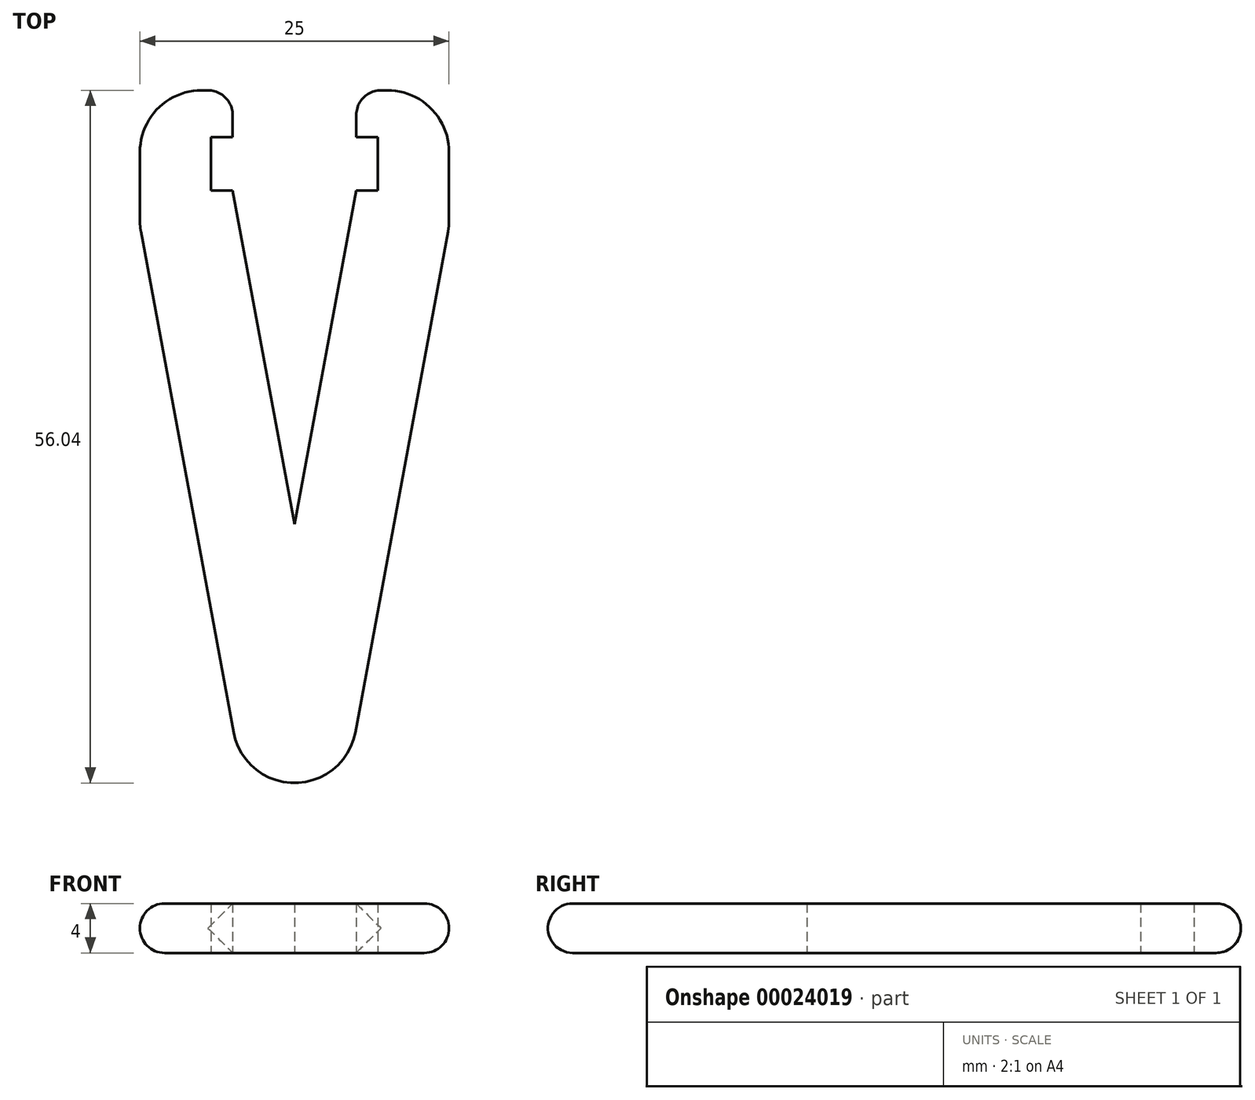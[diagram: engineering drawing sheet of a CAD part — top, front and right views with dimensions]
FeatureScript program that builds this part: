
annotation { "Feature Type Name" : "Feature", "Feature Type Description" : "" }
export const myFeature = defineFeature(function(context is Context, id is Id, definition is map)
    precondition{}
    {
        {
            var Q0;
            Q0=qCreatedBy(makeId("Top.planeOp"),FACE);
            var sketch = newSketch(context, id + "F0", { "sketchPlane" : qUnion([Q0])});
            skLineSegment(sketch, "E0.rect.bottom", {"start": v(6.75, -2.15) * mm, "end": v(-6.75, -2.15) * mm});
            skLineSegment(sketch, "E0.rect.top", {"start": v(6.75, 2.15) * mm, "end": v(-6.75, 2.15) * mm});
            skLineSegment(sketch, "E0.rect.left", {"start": v(6.75, -2.15) * mm, "end": v(6.75, 2.15) * mm});
            skLineSegment(sketch, "E0.rect.right", {"start": v(-6.75, -2.15) * mm, "end": v(-6.75, 2.15) * mm});
            skPoint(sketch, "E0.rect.middle", {"position": v(0, 0) * mm});
            skLineSegment(sketch, "E1", {"start": v(0, -2.15) * mm, "end": v(0, -29.15) * mm, "construction": true});
            skLineSegment(sketch, "E2", {"start": v(0, -2.15) * mm, "end": v(-5, -2.15) * mm});
            skLineSegment(sketch, "E3", {"start": v(0, 0) * mm, "end": v(0, 8.22) * mm, "construction": true});
            skLineSegment(sketch, "E4", {"start": v(0, 0) * mm, "end": v(-18.96, 0) * mm, "construction": true});
            skLineSegment(sketch, "E5.MirrorCS", {"start": v(0, 2.15) * mm, "end": v(-5, 2.15) * mm});
            skLineSegment(sketch, "E6", {"start": v(-5, 2.15) * mm, "end": v(-5, 5.95) * mm});
            skLineSegment(sketch, "E7", {"start": v(-5, -2.15) * mm, "end": v(0, -29.15) * mm});
            skLineSegment(sketch, "E8", {"start": v(-5, 5.95) * mm, "end": v(-12.5, 5.95) * mm});
            skLineSegment(sketch, "E9", {"start": v(-12.5, 5.95) * mm, "end": v(-12.5, -5.05) * mm});
            skLineSegment(sketch, "E10", {"start": v(-12.5, -5.05) * mm, "end": v(0, -72.55) * mm});
            skLineSegment(sketch, "E11", {"start": v(0, -29.15) * mm, "end": v(0, -98.8) * mm, "construction": true});
            skLineSegment(sketch, "E12.MirrorCS", {"start": v(5, -2.15) * mm, "end": v(0, -29.15) * mm});
            skLineSegment(sketch, "E13.MirrorCS", {"start": v(5, 5.95) * mm, "end": v(12.5, 5.95) * mm});
            skLineSegment(sketch, "E14.MirrorCS", {"start": v(5, 2.15) * mm, "end": v(5, 5.95) * mm});
            skLineSegment(sketch, "E15.MirrorCS", {"start": v(12.5, 5.95) * mm, "end": v(12.5, -5.05) * mm});
            skLineSegment(sketch, "E16.MirrorCS", {"start": v(12.5, -5.05) * mm, "end": v(0, -72.55) * mm});
            skSolve(sketch);
        }
        {
            var Q0;
            {var subQ4=sQuery(id+"F0.wireOp",EDGE,"E0.rect.left");Q0=makeQuery(id+"F0.imprint","IMPRINT",FACE,{"disambiguationData":[TD([[makeQuery(id+"F0.imprint","IMPRINT",EDGE,{"derivedFrom":subQ4}),-1.0]])]});}
            extrude(context, id + "F1", {"entities" : qUnion([Q0]), "depth" : 4 * mm});
        }
        {
            var Q0;
            Q0=makeQuery(id+"F1.opExtrude","SWEPT_EDGE",EDGE,{"disambiguationData":[OSD([sQuery(id+"F0.wireOp",EDGE,"E10"),sQuery(id+"F0.wireOp",EDGE,"E16.MirrorCS")])]});
            fillet(context, id + "F2", {"entities" : qUnion([Q0]), "radius" : 5 * mm, "tangentPropagation" : true, "allowEdgeOverflow" : false});
        }
        {
            var Q0;
            Q0=makeQuery(id+"F1.opExtrude","SWEPT_EDGE",EDGE,{"disambiguationData":[OSD([sQuery(id+"F0.wireOp",EDGE,"E9"),sQuery(id+"F0.wireOp",EDGE,"E10")])]});
            var Q1;
            Q1=makeQuery(id+"F1.opExtrude","SWEPT_EDGE",EDGE,{"disambiguationData":[OSD([sQuery(id+"F0.wireOp",EDGE,"E8"),sQuery(id+"F0.wireOp",EDGE,"E9")])]});
            var Q2;
            Q2=makeQuery(id+"F1.opExtrude","SWEPT_EDGE",EDGE,{"disambiguationData":[OSD([sQuery(id+"F0.wireOp",EDGE,"E13.MirrorCS"),sQuery(id+"F0.wireOp",EDGE,"E15.MirrorCS")])]});
            var Q3;
            Q3=makeQuery(id+"F1.opExtrude","SWEPT_EDGE",EDGE,{"disambiguationData":[OSD([sQuery(id+"F0.wireOp",EDGE,"E15.MirrorCS"),sQuery(id+"F0.wireOp",EDGE,"E16.MirrorCS")])]});
            fillet(context, id + "F3", {"entities" : qUnion([Q0, Q1, Q2, Q3]), "radius" : 5 * mm, "tangentPropagation" : true, "allowEdgeOverflow" : false});
        }
        {
            var Q0;
            Q0=makeQuery(id+"F1.opExtrude","SWEPT_EDGE",EDGE,{"disambiguationData":[OSD([sQuery(id+"F0.wireOp",EDGE,"E6"),sQuery(id+"F0.wireOp",EDGE,"E8")])]});
            var Q1;
            Q1=makeQuery(id+"F1.opExtrude","SWEPT_EDGE",EDGE,{"disambiguationData":[OSD([sQuery(id+"F0.wireOp",EDGE,"E13.MirrorCS"),sQuery(id+"F0.wireOp",EDGE,"E14.MirrorCS")])]});
            var Q2;
            Q2=makeQuery(id+"F1.opExtrude","SWEPT_FACE",FACE,{"disambiguationData":[OSD([sQuery(id+"F0.wireOp",EDGE,"E16.MirrorCS")])]});
            fillet(context, id + "F4", {"entities" : qUnion([Q0, Q1, Q2]), "radius" : 2 * mm, "tangentPropagation" : true, "allowEdgeOverflow" : false});
        }
    });
